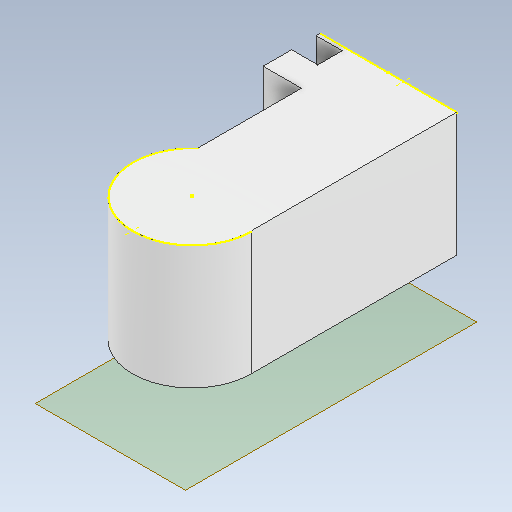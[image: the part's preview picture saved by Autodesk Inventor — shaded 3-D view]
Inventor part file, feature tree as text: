
AUTODESK INVENTOR PART (.ipt)
format: ipt  version: 2021 (Build 250183000, 183)  size: 124,416 bytes
history: native  units: mm
features: other x3, sketch x2, plane x1
ambient origin geometry x8: Origin, YZ Plane, XZ Plane, XY Plane, X Axis, Y Axis, Z Axis, Center Point
bodies: Solid1 (feature_tree)
feature tree (6):
  other  "Legs final (2).ipt"
  other  "Solid1::Legs final (2).ipt"
  other  "TaggingFeature1"
  sketch  "Sketch5"  dims[d0=30.0mm]
  sketch  "Sketch11"
  plane  "Work Plane1"
